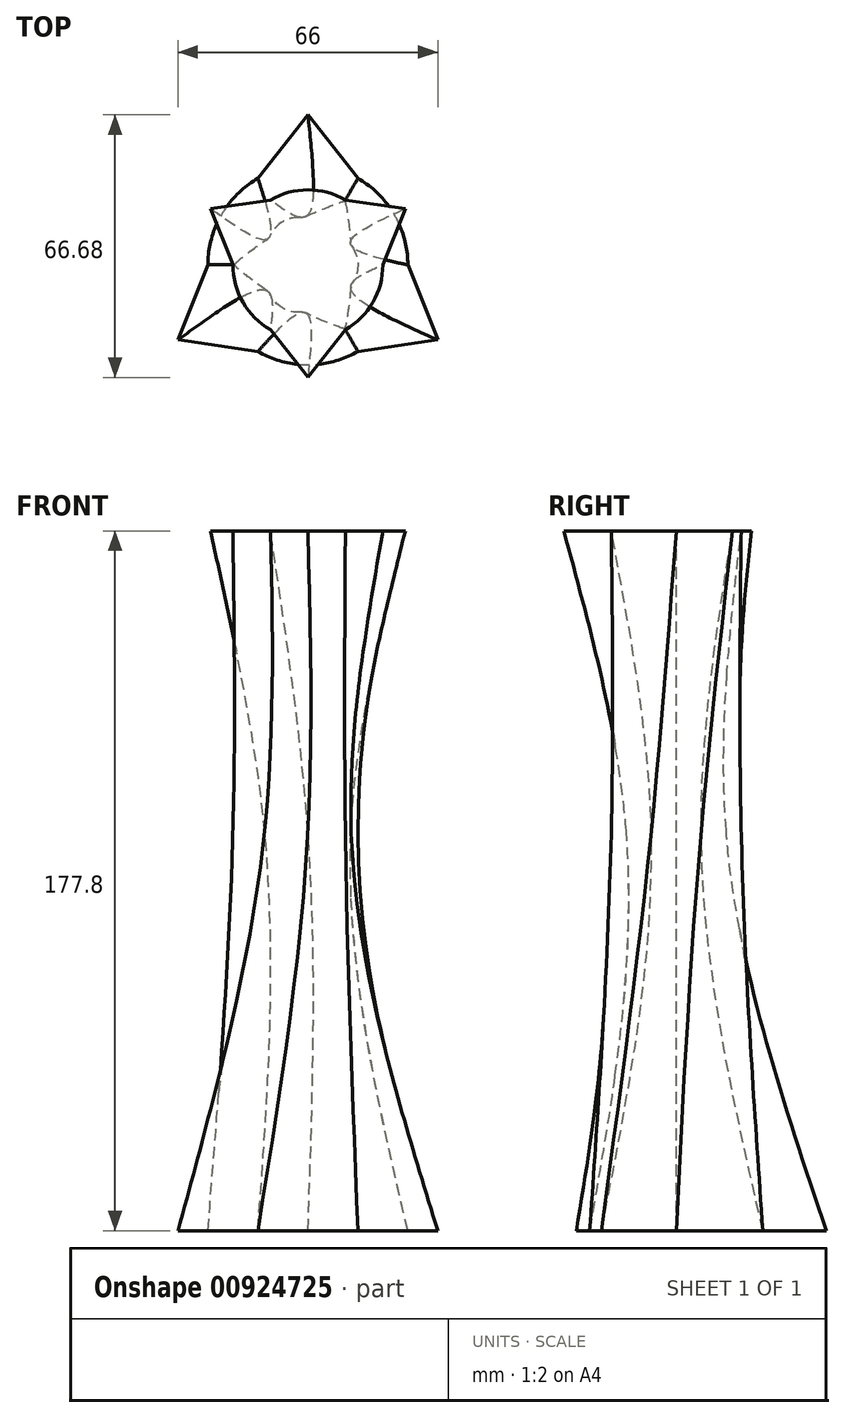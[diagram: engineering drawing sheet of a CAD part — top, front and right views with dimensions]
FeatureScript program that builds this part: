
annotation { "Feature Type Name" : "Feature", "Feature Type Description" : "" }
export const myFeature = defineFeature(function(context is Context, id is Id, definition is map)
    precondition{}
    {
        {
            var Q0;
            Q0=qCreatedBy(makeId("Top.planeOp"),FACE);
            var sketch = newSketch(context, id + "F0", { "sketchPlane" : qUnion([Q0])});
            skArc(sketch, "E0", {"start": v(-12.7, 22) * mm, "mid": v(-22, 12.7) * mm, "end": v(-25.4, 0) * mm});
            skLineSegment(sketch, "E1", {"start": v(0, 38.1) * mm, "end": v(12.7, 22) * mm});
            skLineSegment(sketch, "E2.MirrorCS", {"start": v(0, 38.1) * mm, "end": v(-12.7, 22) * mm});
            skLineSegment(sketch, "E3.1.0", {"start": v(-33, -19.05) * mm, "end": v(-25.4, 0) * mm});
            skLineSegment(sketch, "E3.1.1", {"start": v(-33, -19.05) * mm, "end": v(-12.7, -22) * mm});
            skLineSegment(sketch, "E3.2.0", {"start": v(33, -19.05) * mm, "end": v(12.7, -22) * mm});
            skLineSegment(sketch, "E3.2.1", {"start": v(33, -19.05) * mm, "end": v(25.4, 0) * mm});
            skArc(sketch, "E4.trimOffspring", {"start": v(-12.7, -22) * mm, "mid": v(0, -25.4) * mm, "end": v(12.7, -22) * mm});
            skArc(sketch, "E5.trimOffspring", {"start": v(25.4, 0) * mm, "mid": v(22, 12.7) * mm, "end": v(12.7, 22) * mm});
            skSolve(sketch);
        }
        {
            var Q0;
            Q0=qCreatedBy(makeId("Top.planeOp"),FACE);
            cPlane(context, id + "F1", {"entities" : qUnion([Q0]), "cplaneType" : CPlaneType.OFFSET, "offset" : 101.6 * mm, "width" : 152.4 * mm, "height" : 152.4 * mm});
        }
        {
            var Q0;
            Q0=qCreatedBy(id+"F1.planeOp",FACE);
            var sketch = newSketch(context, id + "F2", { "sketchPlane" : qUnion([Q0])});
            skArc(sketch, "E6", {"start": v(-11, -6.35) * mm, "mid": v(-6.35, -11) * mm, "end": v(0, -12.7) * mm});
            skLineSegment(sketch, "E7", {"start": v(-19.05, 0) * mm, "end": v(-11, -6.35) * mm});
            skLineSegment(sketch, "E8.MirrorCS", {"start": v(-19.05, 0) * mm, "end": v(-11, 6.35) * mm});
            skLineSegment(sketch, "E9.1.0", {"start": v(9.53, -16.5) * mm, "end": v(0, -12.7) * mm});
            skLineSegment(sketch, "E9.1.1", {"start": v(9.52, -16.5) * mm, "end": v(11, -6.35) * mm});
            skLineSegment(sketch, "E9.2.0", {"start": v(9.53, 16.5) * mm, "end": v(11, 6.35) * mm});
            skLineSegment(sketch, "E9.2.1", {"start": v(9.53, 16.5) * mm, "end": v(0, 12.7) * mm});
            skArc(sketch, "E10.trimOffspring", {"start": v(11, -6.35) * mm, "mid": v(12.7, 0) * mm, "end": v(11, 6.35) * mm});
            skArc(sketch, "E11.trimOffspring", {"start": v(0, 12.7) * mm, "mid": v(-6.35, 11) * mm, "end": v(-11, 6.35) * mm});
            skSolve(sketch);
        }
        {
            var Q0;
            Q0=qCreatedBy(id+"F1.planeOp",FACE);
            cPlane(context, id + "F3", {"entities" : qUnion([Q0]), "cplaneType" : CPlaneType.OFFSET, "offset" : 76.2 * mm, "width" : 152.4 * mm, "height" : 152.4 * mm});
        }
        {
            var Q0;
            Q0=qCreatedBy(id+"F3.planeOp",FACE);
            var sketch = newSketch(context, id + "F4", { "sketchPlane" : qUnion([Q0])});
            skArc(sketch, "E12", {"start": v(9.53, 16.5) * mm, "mid": v(0, 19.05) * mm, "end": v(-9.52, 16.5) * mm});
            skLineSegment(sketch, "E13", {"start": v(0, -28.58) * mm, "end": v(9.53, -16.5) * mm});
            skLineSegment(sketch, "E14.MirrorCS", {"start": v(0, -28.58) * mm, "end": v(-9.53, -16.5) * mm});
            skLineSegment(sketch, "E15.1.0", {"start": v(24.75, 14.29) * mm, "end": v(9.52, 16.5) * mm});
            skLineSegment(sketch, "E15.1.1", {"start": v(24.75, 14.29) * mm, "end": v(19.05, 0) * mm});
            skLineSegment(sketch, "E15.2.0", {"start": v(-24.75, 14.29) * mm, "end": v(-19.05, 0) * mm});
            skLineSegment(sketch, "E15.2.1", {"start": v(-24.75, 14.29) * mm, "end": v(-9.52, 16.5) * mm});
            skArc(sketch, "E16.trimOffspring", {"start": v(9.53, -16.5) * mm, "mid": v(16.5, -9.53) * mm, "end": v(19.05, 0) * mm});
            skArc(sketch, "E17.trimOffspring", {"start": v(-19.05, 0) * mm, "mid": v(-16.5, -9.52) * mm, "end": v(-9.53, -16.5) * mm});
            skSolve(sketch);
        }
        {
            var Q0;
            Q0=makeQuery(id+"F0.imprint","IMPRINT",FACE,{"disambiguationData":[TD([[makeQuery(id+"F0.imprint","IMPRINT",EDGE,{"derivedFrom":sQuery(id+"F0.wireOp",EDGE,"E0")}),1.0]])]});
            var Q1;
            Q1=makeQuery(id+"F2.imprint","IMPRINT",FACE,{"disambiguationData":[TD([[makeQuery(id+"F2.imprint","IMPRINT",EDGE,{"derivedFrom":sQuery(id+"F2.wireOp",EDGE,"E6")}),1.0]])]});
            var Q2;
            Q2=makeQuery(id+"F4.imprint","IMPRINT",FACE,{"disambiguationData":[TD([[makeQuery(id+"F4.imprint","IMPRINT",EDGE,{"derivedFrom":sQuery(id+"F4.wireOp",EDGE,"E12")}),1.0]])]});
            loft(context, id + "F5", {"sheetProfilesArray" : [{ "sheetProfileEntities" : qUnion([Q0]) }, { "sheetProfileEntities" : qUnion([Q1]) }, { "sheetProfileEntities" : qUnion([Q2]) }]});
        }
    });
